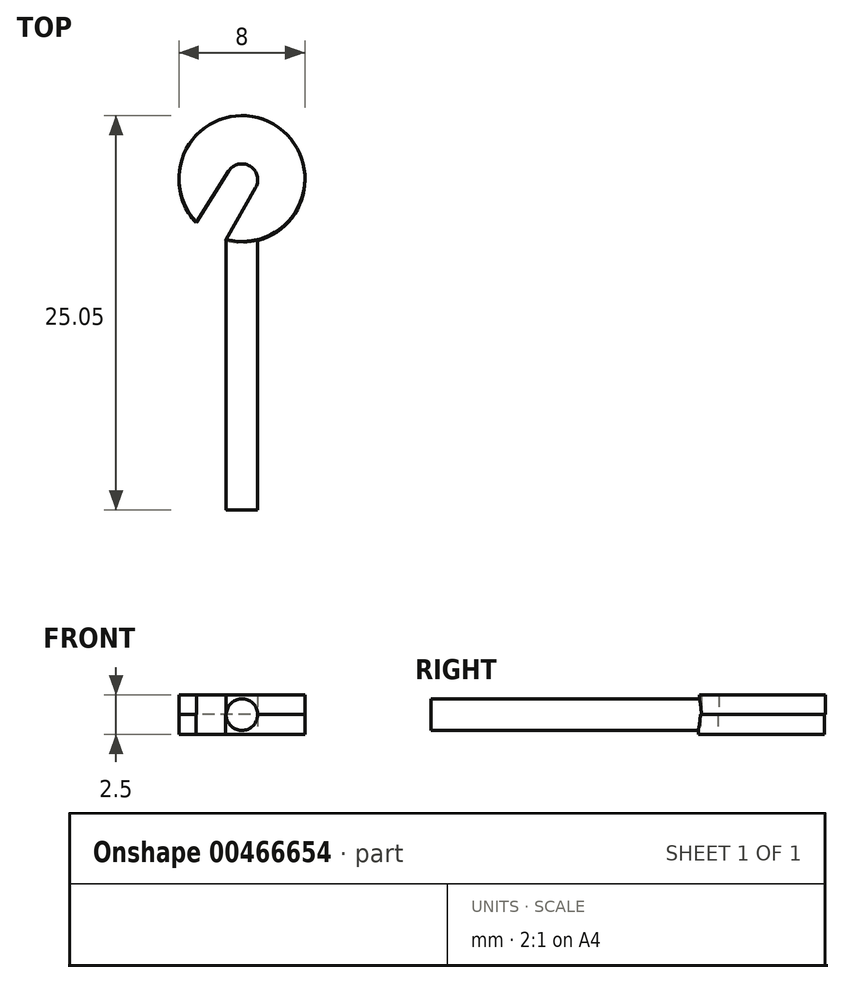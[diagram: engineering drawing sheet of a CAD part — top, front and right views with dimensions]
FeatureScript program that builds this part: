
annotation { "Feature Type Name" : "Feature", "Feature Type Description" : "" }
export const myFeature = defineFeature(function(context is Context, id is Id, definition is map)
    precondition{}
    {
        {
            var Q0;
            Q0=qCreatedBy(makeId("Front.planeOp"),FACE);
            var sketch = newSketch(context, id + "F0", { "sketchPlane" : qUnion([Q0])});
            skCircle(sketch, "E0", {"center": v(0, 0) * mm, "radius": 1 * mm});
            skSolve(sketch);
        }
        {
            var Q0;
            Q0 = qSketchRegion(id + "F0", true);
            extrude(context, id + "F1", {"entities" : qUnion([Q0]), "depth" : 19.05 * mm});
        }
        {
            var Q0;
            Q0=qCreatedBy(makeId("Top.planeOp"),FACE);
            var sketch = newSketch(context, id + "F2", { "sketchPlane" : qUnion([Q0])});
            skPoint(sketch, "E1", {"position": v(0, 4) * mm});
            skPoint(sketch, "E2", {"position": v(0, 2) * mm});
            skCircle(sketch, "E3", {"center": v(0, 2) * mm, "radius": 4 * mm});
            skSolve(sketch);
        }
        {
            var Q0;
            Q0 = qSketchRegion(id + "F2", true);
            extrude(context, id + "F3", {"entities" : qUnion([Q0]), "operationType" : NewBodyOperationType.ADD, "depth" : 1.25 * mm});
        }
        {
            var Q0;
            Q0=qCreatedBy(makeId("Top.planeOp"),FACE);
            var sketch = newSketch(context, id + "F4", { "sketchPlane" : qUnion([Q0])});
            skPoint(sketch, "E4", {"position": v(0, 3.93) * mm});
            skPoint(sketch, "E5", {"position": v(0, 1.93) * mm});
            skCircle(sketch, "E6", {"center": v(0, 1.93) * mm, "radius": 4 * mm});
            skSolve(sketch);
        }
        {
            var Q0;
            Q0 = qSketchRegion(id + "F4", true);
            extrude(context, id + "F5", {"entities" : qUnion([Q0]), "operationType" : NewBodyOperationType.ADD, "oppositeDirection" : true, "depth" : 1.25 * mm});
        }
        {
            var Q0;
            Q0=makeQuery(id+"F5.opExtrude","CAP_FACE",FACE,{"disambiguationData":[OSD([sQuery(id+"F4.wireOp",EDGE,"E6")])],"isStart":false});
            var sketch = newSketch(context, id + "F6", { "sketchPlane" : qUnion([Q0])});
            skPoint(sketch, "E7", {"position": v(0, -1.93) * mm});
            skCircle(sketch, "E8", {"center": v(0, -1.93) * mm, "radius": 1 * mm});
            skLineSegment(sketch, "E9", {"start": v(-1.03, 1.93) * mm, "end": v(0.87, -1.44) * mm});
            skLineSegment(sketch, "E10", {"start": v(-0.85, -2.47) * mm, "end": v(0.87, -1.44) * mm});
            skLineSegment(sketch, "E11", {"start": v(-0.85, -2.47) * mm, "end": v(-2.91, 0.8) * mm});
            skSolve(sketch);
        }
        {
            var Q0;
            Q0 = qSketchRegion(id + "F6", true);
            extrude(context, id + "F7", {"entities" : qUnion([Q0]), "operationType" : NewBodyOperationType.REMOVE, "oppositeDirection" : true, "depth" : 25 * mm});
        }
        {
            var Q0;
            {var subQ1=sQuery(id+"F6.wireOp",EDGE,"E9");Q0=makeQuery(id+"F6.imprint","IMPRINT",FACE,{"disambiguationData":[TD([[makeQuery(id+"F6.imprint","IMPRINT",EDGE,{"derivedFrom":subQ1}),-1.0]])]});}
            extrude(context, id + "F8", {"entities" : qUnion([Q0]), "operationType" : NewBodyOperationType.REMOVE, "oppositeDirection" : true, "depth" : 25 * mm});
        }
    });
